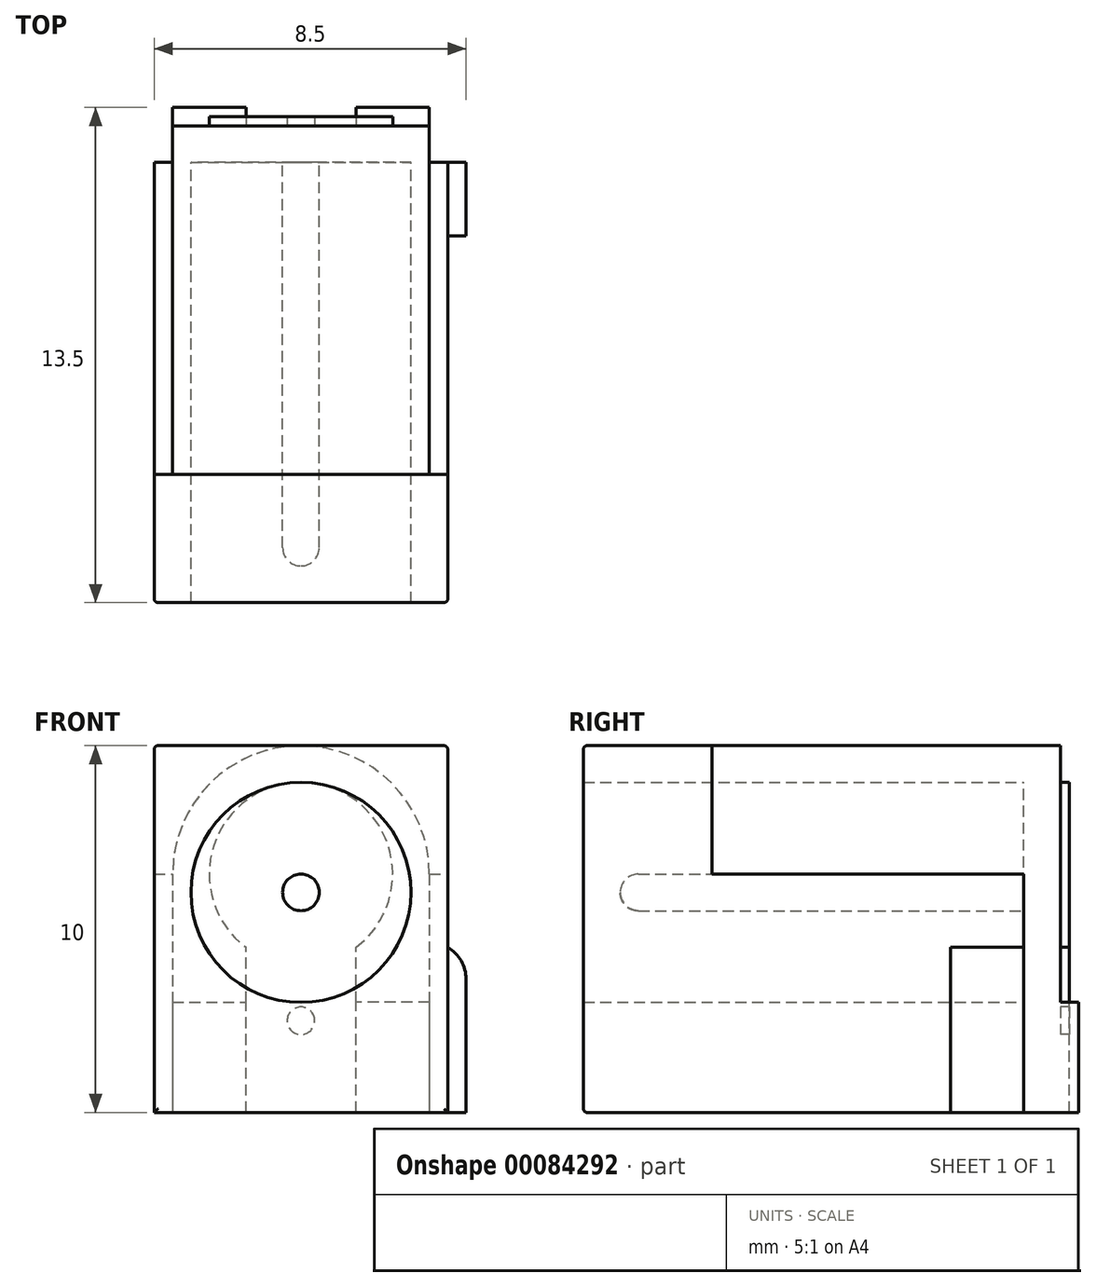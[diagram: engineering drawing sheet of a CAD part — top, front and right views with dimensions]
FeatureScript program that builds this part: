
annotation { "Feature Type Name" : "Feature", "Feature Type Description" : "" }
export const myFeature = defineFeature(function(context is Context, id is Id, definition is map)
    precondition{}
    {
        {
            var Q0;
            Q0=qCreatedBy(makeId("Front.planeOp"),FACE);
            var sketch = newSketch(context, id + "F0", { "sketchPlane" : qUnion([Q0])});
            skLineSegment(sketch, "E0.bottom", {"start": v(-33.98, 12.36) * mm, "end": v(-25.98, 12.36) * mm});
            skLineSegment(sketch, "E0.top", {"start": v(-33.98, 2.36) * mm, "end": v(-25.98, 2.36) * mm});
            skLineSegment(sketch, "E0.left", {"start": v(-33.98, 12.36) * mm, "end": v(-33.98, 2.36) * mm});
            skLineSegment(sketch, "E0.right", {"start": v(-25.98, 12.36) * mm, "end": v(-25.98, 2.36) * mm});
            skCircle(sketch, "E1", {"center": v(-29.98, 8.36) * mm, "radius": 3 * mm});
            skPoint(sketch, "E1.centerSnap0", {"position": v(-29.98, 12.36) * mm});
            skSolve(sketch);
        }
        {
            var Q0;
            Q0=makeQuery(id+"F0.imprint","IMPRINT",FACE,{"disambiguationData":[TD([[makeQuery(id+"F0.imprint","IMPRINT",EDGE,{"derivedFrom":sQuery(id+"F0.wireOp",EDGE,"E0.bottom")}),-1.0]])]});
            extrude(context, id + "F1", {"entities" : qUnion([Q0]), "depth" : 12 * mm});
        }
        {
            var Q0;
            Q0=makeQuery(id+"F1.opExtrude","SWEPT_FACE",FACE,{"disambiguationData":[OSD([sQuery(id+"F0.wireOp",EDGE,"E0.left")])]});
            var sketch = newSketch(context, id + "F2", { "sketchPlane" : qUnion([Q0])});
            skLineSegment(sketch, "E2.bottom", {"start": v(0, 12.36) * mm, "end": v(-1, 12.36) * mm});
            skLineSegment(sketch, "E2.top", {"start": v(0, 2.36) * mm, "end": v(-1, 2.36) * mm});
            skLineSegment(sketch, "E2.left", {"start": v(0, 12.36) * mm, "end": v(0, 2.36) * mm});
            skLineSegment(sketch, "E2.right", {"start": v(-1, 12.36) * mm, "end": v(-1, 2.36) * mm});
            skSolve(sketch);
        }
        {
            var Q0;
            Q0 = qSketchRegion(id + "F2", true);
            var Q1;
            Q1=makeQuery(id+"F1.opExtrude","SWEPT_FACE",FACE,{"disambiguationData":[OSD([sQuery(id+"F0.wireOp",EDGE,"E0.right")])]});
            extrude(context, id + "F3", {"entities" : qUnion([Q0]), "operationType" : NewBodyOperationType.ADD, "endBound" : BoundingType.UP_TO_SURFACE, "oppositeDirection" : true, "endBoundEntityFace" : qUnion([Q1]), "depth" : 25 * mm});
        }
        {
            var Q0;
            Q0=makeQuery(id+"F3.opExtrude","SWEPT_FACE",FACE,{"disambiguationData":[OSD([sQuery(id+"F2.wireOp",EDGE,"E2.right")])]});
            var sketch = newSketch(context, id + "F4", { "sketchPlane" : qUnion([Q0])});
            skLineSegment(sketch, "E3", {"start": v(25.98, 12.36) * mm, "end": v(33.98, 12.36) * mm});
            skLineSegment(sketch, "E4", {"start": v(29.98, 12.36) * mm, "end": v(29.98, 8.86) * mm});
            skCircle(sketch, "E5", {"center": v(29.98, 8.86) * mm, "radius": 3.5 * mm});
            skLineSegment(sketch, "E6", {"start": v(33.98, 8.86) * mm, "end": v(25.98, 8.86) * mm});
            skLineSegment(sketch, "E7", {"start": v(26.48, 8.86) * mm, "end": v(26.48, 2.36) * mm});
            skLineSegment(sketch, "E8", {"start": v(33.48, 8.86) * mm, "end": v(33.48, 2.36) * mm});
            skSolve(sketch);
        }
        {
            var Q0;
            {var subQ0=sQuery(id+"F4.wireOp",EDGE,"E3");var subQ1=makeQuery(id+"F3.opExtrude","CAP_EDGE",EDGE,{"disambiguationData":[OSD([sQuery(id+"F2.wireOp",EDGE,"E2.right")])],"isStart":true});var subQ2=makeQuery(id+"F4.imprint","INTERSECT",VERTEX,{"derivedFrom":[subQ1,subQ0]});Q0=makeQuery(id+"F4.imprint","IMPRINT",FACE,{"disambiguationData":[TD([[makeQuery(id+"F4.imprint","IMPRINT",EDGE,{"disambiguationData":[TD([[subQ2,-1.0]])],"derivedFrom":subQ1}),-1.0]])]});}
            var Q1;
            {var subQ0=sQuery(id+"F4.wireOp",EDGE,"E3");var subQ1=makeQuery(id+"F3.opExtrude","TWEAK_EDGE",EDGE,{"derivedFrom":[makeQuery(id+"F1.opExtrude","SWEPT_FACE",FACE,{"disambiguationData":[OSD([sQuery(id+"F0.wireOp",EDGE,"E0.right")])]}),makeQuery(id+"F2.imprint","IMPRINT",EDGE,{"derivedFrom":sQuery(id+"F2.wireOp",EDGE,"E2.right")})]});var subQ2=makeQuery(id+"F4.imprint","INTERSECT",VERTEX,{"derivedFrom":[subQ1,subQ0]});Q1=makeQuery(id+"F4.imprint","IMPRINT",FACE,{"disambiguationData":[TD([[makeQuery(id+"F4.imprint","IMPRINT",EDGE,{"disambiguationData":[TD([[subQ2,-1.0]])],"derivedFrom":subQ0}),-1.0]])]});}
            extrude(context, id + "F5", {"entities" : qUnion([Q0, Q1]), "operationType" : NewBodyOperationType.REMOVE, "oppositeDirection" : true, "depth" : 9.5 * mm});
        }
        {
            var Q0;
            {var subQ4=sQuery(id+"F4.wireOp",EDGE,"E7");Q0=makeQuery(id+"F4.imprint","IMPRINT",FACE,{"disambiguationData":[TD([[makeQuery(id+"F4.imprint","IMPRINT",EDGE,{"derivedFrom":subQ4}),-1.0]])]});}
            var Q1;
            {var subQ4=sQuery(id+"F4.wireOp",EDGE,"E8");Q1=makeQuery(id+"F4.imprint","IMPRINT",FACE,{"disambiguationData":[TD([[makeQuery(id+"F4.imprint","IMPRINT",EDGE,{"derivedFrom":subQ4}),1.0]])]});}
            extrude(context, id + "F6", {"entities" : qUnion([Q0, Q1]), "operationType" : NewBodyOperationType.REMOVE, "oppositeDirection" : true, "depth" : 1 * mm});
        }
        {
            var Q0;
            Q0=makeQuery(id+"F3.opExtrude","SWEPT_FACE",FACE,{"disambiguationData":[OSD([sQuery(id+"F2.wireOp",EDGE,"E2.left")])]});
            var sketch = newSketch(context, id + "F7", { "sketchPlane" : qUnion([Q0])});
            skCircle(sketch, "E9", {"center": v(-29.98, 8.36) * mm, "radius": 0.5 * mm});
            skSolve(sketch);
        }
        {
            var Q0;
            Q0 = qSketchRegion(id + "F7", true);
            extrude(context, id + "F8", {"entities" : qUnion([Q0]), "operationType" : NewBodyOperationType.ADD, "depth" : 11 * mm});
        }
        {
            var Q0;
            Q0=makeQuery(id+"F8.opExtrude","CAP_EDGE",EDGE,{"disambiguationData":[OSD([sQuery(id+"F7.wireOp",EDGE,"E9")])],"isStart":false});
            fillet(context, id + "F9", {"entities" : qUnion([Q0]), "radius" : 0.5 * mm, "tangentPropagation" : true, "allowEdgeOverflow" : false});
        }
        {
            var Q0;
            Q0=makeQuery(id+"F1.opExtrude","CAP_EDGE",EDGE,{"disambiguationData":[OSD([sQuery(id+"F0.wireOp",EDGE,"E0.bottom")])],"isStart":false});
            var Q1;
            Q1=makeQuery(id+"F1.opExtrude","CAP_EDGE",EDGE,{"disambiguationData":[OSD([sQuery(id+"F0.wireOp",EDGE,"E0.right")])],"isStart":false});
            var Q2;
            Q2=makeQuery(id+"F1.opExtrude","CAP_EDGE",EDGE,{"disambiguationData":[OSD([sQuery(id+"F0.wireOp",EDGE,"E0.left")])],"isStart":false});
            var Q3;
            Q3=makeQuery(id+"F1.opExtrude","CAP_EDGE",EDGE,{"disambiguationData":[OSD([sQuery(id+"F0.wireOp",EDGE,"E0.top")])],"isStart":false});
            var Q4;
            {var subQ0=sQuery(id+"F0.wireOp",EDGE,"E0.right");Q4=makeQuery(id+"F3.boolean.opBoolean","MERGE",EDGE,{"derivedFrom":[makeQuery(id+"F1.opExtrude","SWEPT_EDGE",EDGE,{"disambiguationData":[OSD([sQuery(id+"F0.wireOp",EDGE,"E0.bottom"),subQ0])]}),makeQuery(id+"F3.opExtrude","TWEAK_EDGE",EDGE,{"derivedFrom":[makeQuery(id+"F1.opExtrude","SWEPT_FACE",FACE,{"disambiguationData":[OSD([subQ0])]}),makeQuery(id+"F2.imprint","IMPRINT",EDGE,{"derivedFrom":sQuery(id+"F2.wireOp",EDGE,"E2.bottom")})]})]});}
            var Q5;
            Q5=makeQuery(id+"F3.boolean.opBoolean","MERGE",EDGE,{"derivedFrom":[makeQuery(id+"F1.opExtrude","SWEPT_EDGE",EDGE,{"disambiguationData":[OSD([sQuery(id+"F0.wireOp",EDGE,"E0.bottom"),sQuery(id+"F0.wireOp",EDGE,"E0.left")])]}),makeQuery(id+"F3.opExtrude","CAP_EDGE",EDGE,{"disambiguationData":[OSD([sQuery(id+"F2.wireOp",EDGE,"E2.bottom")])],"isStart":true})]});
            fillet(context, id + "F10", {"entities" : qUnion([Q0, Q1, Q2, Q3, Q4, Q5]), "radius" : 0.1 * mm, "tangentPropagation" : true, "allowEdgeOverflow" : false});
        }
        {
            var Q0;
            Q0=makeQuery(id+"F3.opExtrude","SWEPT_FACE",FACE,{"disambiguationData":[OSD([sQuery(id+"F2.wireOp",EDGE,"E2.right")])]});
            var sketch = newSketch(context, id + "F11", { "sketchPlane" : qUnion([Q0])});
            skLineSegment(sketch, "E10.bottom", {"start": v(26.48, 2.36) * mm, "end": v(28.48, 2.36) * mm});
            skLineSegment(sketch, "E10.top", {"start": v(26.48, 5.36) * mm, "end": v(28.48, 5.36) * mm});
            skLineSegment(sketch, "E10.left", {"start": v(26.48, 2.36) * mm, "end": v(26.48, 5.36) * mm});
            skLineSegment(sketch, "E10.right", {"start": v(28.48, 2.36) * mm, "end": v(28.48, 5.36) * mm});
            skLineSegment(sketch, "E11.bottom", {"start": v(33.48, 2.36) * mm, "end": v(31.48, 2.36) * mm});
            skLineSegment(sketch, "E11.top", {"start": v(33.48, 5.36) * mm, "end": v(31.48, 5.36) * mm});
            skLineSegment(sketch, "E11.left", {"start": v(33.48, 2.36) * mm, "end": v(33.48, 5.36) * mm});
            skLineSegment(sketch, "E11.right", {"start": v(31.48, 2.36) * mm, "end": v(31.48, 5.36) * mm});
            skSolve(sketch);
        }
        {
            var Q0;
            Q0 = qSketchRegion(id + "F11", true);
            extrude(context, id + "F12", {"entities" : qUnion([Q0]), "operationType" : NewBodyOperationType.ADD, "depth" : 0.5 * mm});
        }
        {
            var Q0;
            Q0=makeQuery(id+"F3.opExtrude","SWEPT_FACE",FACE,{"disambiguationData":[OSD([sQuery(id+"F2.wireOp",EDGE,"E2.right")])]});
            var sketch = newSketch(context, id + "F13", { "sketchPlane" : qUnion([Q0])});
            skCircle(sketch, "E12", {"center": v(29.98, 8.86) * mm, "radius": 2.5 * mm});
            skLineSegment(sketch, "E13", {"start": v(28.48, 2.36) * mm, "end": v(28.48, 6.86) * mm});
            skLineSegment(sketch, "E14", {"start": v(28.48, 6.86) * mm, "end": v(31.48, 6.86) * mm});
            skLineSegment(sketch, "E15", {"start": v(31.48, 6.86) * mm, "end": v(31.48, 2.36) * mm});
            skCircle(sketch, "E16", {"center": v(29.98, 4.86) * mm, "radius": 0.38 * mm});
            skSolve(sketch);
        }
        {
            var Q0;
            {var subQ0=sQuery(id+"F13.wireOp",EDGE,"E14");Q0=makeQuery(id+"F13.imprint","IMPRINT",FACE,{"disambiguationData":[TD([[makeQuery(id+"F13.imprint","IMPRINT",EDGE,{"derivedFrom":subQ0}),-1.0]])]});}
            var Q1;
            {var subQ0=sQuery(id+"F13.wireOp",EDGE,"E14");Q1=makeQuery(id+"F13.imprint","IMPRINT",FACE,{"disambiguationData":[TD([[makeQuery(id+"F13.imprint","IMPRINT",EDGE,{"derivedFrom":subQ0}),1.0]])]});}
            var Q2;
            Q2=makeQuery(id+"F13.imprint","IMPRINT",FACE,{"disambiguationData":[TD([[makeQuery(id+"F13.imprint","IMPRINT",EDGE,{"derivedFrom":sQuery(id+"F13.wireOp",EDGE,"E16")}),-1.0]])]});
            extrude(context, id + "F14", {"entities" : qUnion([Q0, Q1, Q2]), "operationType" : NewBodyOperationType.ADD, "depth" : 0.25 * mm});
        }
        {
            var Q0;
            {var subQ0=sQuery(id+"F0.wireOp",EDGE,"E0.right");Q0=makeQuery(id+"F3.boolean.opBoolean","MERGE",FACE,{"derivedFrom":[makeQuery(id+"F1.opExtrude","SWEPT_FACE",FACE,{"disambiguationData":[OSD([subQ0])]}),makeQuery(id+"F3.opExtrude","CAP_FACE",FACE,{"disambiguationData":[OSD([subQ0])],"isStart":false})]});}
            var sketch = newSketch(context, id + "F15", { "sketchPlane" : qUnion([Q0])});
            skLineSegment(sketch, "E17.bottom", {"start": v(0, 2.36) * mm, "end": v(-2, 2.36) * mm});
            skLineSegment(sketch, "E17.top", {"start": v(0, 6.86) * mm, "end": v(-2, 6.86) * mm});
            skLineSegment(sketch, "E17.left", {"start": v(0, 2.36) * mm, "end": v(0, 6.86) * mm});
            skLineSegment(sketch, "E17.right", {"start": v(-2, 2.36) * mm, "end": v(-2, 6.86) * mm});
            skSolve(sketch);
        }
        {
            var Q0;
            Q0 = qSketchRegion(id + "F15", true);
            extrude(context, id + "F16", {"entities" : qUnion([Q0]), "operationType" : NewBodyOperationType.ADD, "depth" : 0.5 * mm});
        }
        {
            var Q0;
            Q0=makeQuery(id+"F16.opExtrude","CAP_EDGE",EDGE,{"disambiguationData":[OSD([sQuery(id+"F15.wireOp",EDGE,"E17.top")])],"isStart":false});
            fillet(context, id + "F17", {"entities" : qUnion([Q0]), "radius" : 1 * mm, "allowEdgeOverflow" : false});
        }
    });
